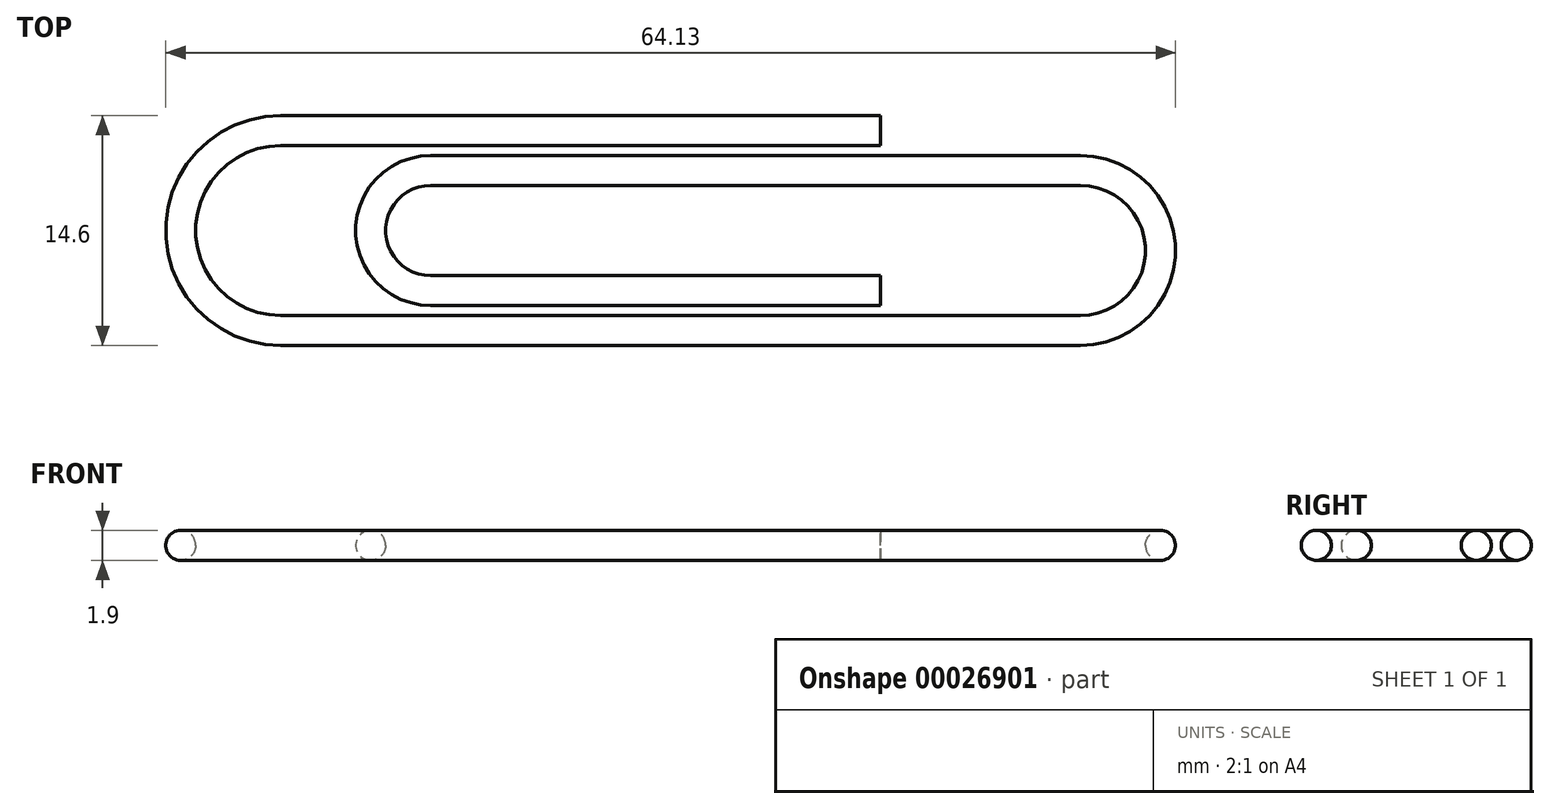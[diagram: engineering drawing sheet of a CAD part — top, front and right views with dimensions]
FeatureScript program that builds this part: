
annotation { "Feature Type Name" : "Feature", "Feature Type Description" : "" }
export const myFeature = defineFeature(function(context is Context, id is Id, definition is map)
    precondition{}
    {
        {
            var Q0;
            Q0=qCreatedBy(makeId("Top.planeOp"),FACE);
            var sketch = newSketch(context, id + "F0", { "sketchPlane" : qUnion([Q0])});
            skLineSegment(sketch, "E0", {"start": v(-1.23, 16.4) * mm, "end": v(-39.33, 16.4) * mm});
            skLineSegment(sketch, "E1", {"start": v(-39.33, 3.7) * mm, "end": v(11.47, 3.7) * mm});
            skArc(sketch, "E2", {"start": v(11.47, 3.7) * mm, "mid": v(16.55, 8.78) * mm, "end": v(11.47, 13.86) * mm});
            skArc(sketch, "E3", {"start": v(-39.33, 16.4) * mm, "mid": v(-45.68, 10.05) * mm, "end": v(-39.33, 3.7) * mm});
            skLineSegment(sketch, "E4", {"start": v(11.47, 13.86) * mm, "end": v(-29.8, 13.86) * mm});
            skArc(sketch, "E5", {"start": v(-29.8, 13.86) * mm, "mid": v(-33.62, 10.05) * mm, "end": v(-29.8, 6.24) * mm});
            skLineSegment(sketch, "E6", {"start": v(-29.8, 6.24) * mm, "end": v(-1.23, 6.24) * mm});
            skSolve(sketch);
        }
        {
            var Q0;
            Q0=sQuery(id+"F0.wireOp",VERTEX,"E0.start");
            var Q1;
            Q1=sQuery(id+"F0.wireOp",EDGE,"E0");
            cPlane(context, id + "F1", {"entities" : qUnion([Q0, Q1]), "cplaneType" : CPlaneType.LINE_POINT, "offset" : 152.4 * mm, "width" : 152.4 * mm, "height" : 152.4 * mm});
        }
        {
            var Q0;
            Q0=qCreatedBy(id+"F1.planeOp",FACE);
            var sketch = newSketch(context, id + "F2", { "sketchPlane" : qUnion([Q0])});
            skPoint(sketch, "E7.0", {"position": v(-16.4, 0) * mm});
            skCircle(sketch, "E8", {"center": v(-16.4, 0) * mm, "radius": 0.95 * mm});
            skSolve(sketch);
        }
        {
            var Q0;
            Q0=makeQuery(id+"F2.imprint","IMPRINT",FACE,{"disambiguationData":[TD([[makeQuery(id+"F2.imprint","IMPRINT",EDGE,{"derivedFrom":sQuery(id+"F2.wireOp",EDGE,"E8")}),1.0]])]});
            var Q1;
            Q1=sQuery(id+"F0.wireOp",EDGE,"E0");
            var Q2;
            Q2=sQuery(id+"F0.wireOp",EDGE,"E3");
            var Q3;
            Q3=sQuery(id+"F0.wireOp",EDGE,"E1");
            var Q4;
            Q4=sQuery(id+"F0.wireOp",EDGE,"E2");
            var Q5;
            Q5=sQuery(id+"F0.wireOp",EDGE,"E4");
            var Q6;
            Q6=sQuery(id+"F0.wireOp",EDGE,"E5");
            var Q7;
            Q7=sQuery(id+"F0.wireOp",EDGE,"E6");
            sweep(context, id + "F3", {"profiles" : qUnion([Q0]), "path" : qUnion([Q1, Q2, Q3, Q4, Q5, Q6, Q7])});
        }
    });
